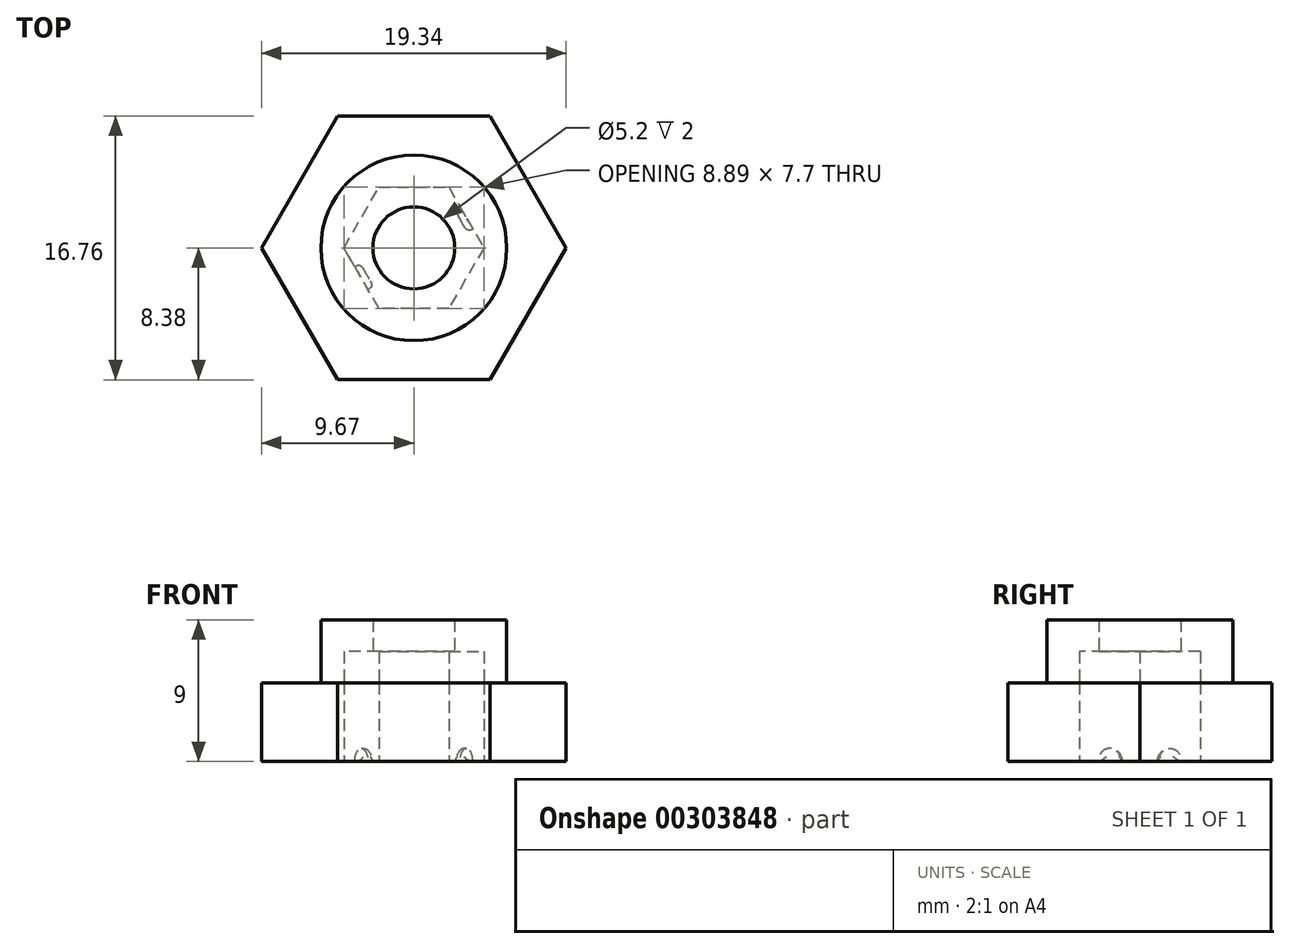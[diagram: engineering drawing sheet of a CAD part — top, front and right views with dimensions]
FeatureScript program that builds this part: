
annotation { "Feature Type Name" : "Feature", "Feature Type Description" : "" }
export const myFeature = defineFeature(function(context is Context, id is Id, definition is map)
    precondition{}
    {
        {
            var Q0;
            Q0=qCreatedBy(makeId("Top.planeOp"),FACE);
            var sketch = newSketch(context, id + "F0", { "sketchPlane" : qUnion([Q0])});
            skCircle(sketch, "E0.cCircle", {"center": v(0, 0) * mm, "radius": 8.38 * mm, "construction": true});
            skLineSegment(sketch, "E0.0", {"start": v(9.67, 0) * mm, "end": v(4.84, -8.38) * mm});
            skLineSegment(sketch, "E0.1", {"start": v(4.84, -8.38) * mm, "end": v(-4.84, -8.37) * mm});
            skLineSegment(sketch, "E0.2", {"start": v(-4.84, -8.38) * mm, "end": v(-9.67, 0) * mm});
            skLineSegment(sketch, "E0.3", {"start": v(-9.67, 0) * mm, "end": v(-4.84, 8.38) * mm});
            skLineSegment(sketch, "E0.4", {"start": v(-4.84, 8.37) * mm, "end": v(4.84, 8.37) * mm});
            skLineSegment(sketch, "E0.5", {"start": v(4.84, 8.38) * mm, "end": v(9.67, 0) * mm});
            skPoint(sketch, "E0.0.midPoint", {"position": v(7.25, -4.19) * mm});
            skCircle(sketch, "E1.cCircle", {"center": v(0, 0) * mm, "radius": 3.85 * mm, "construction": true});
            skLineSegment(sketch, "E1.0", {"start": v(4.45, 0) * mm, "end": v(2.22, -3.85) * mm});
            skLineSegment(sketch, "E1.1", {"start": v(2.22, -3.85) * mm, "end": v(-2.22, -3.85) * mm});
            skLineSegment(sketch, "E1.2", {"start": v(-2.22, -3.85) * mm, "end": v(-4.45, 0) * mm});
            skLineSegment(sketch, "E1.3", {"start": v(-4.45, 0) * mm, "end": v(-2.22, 3.85) * mm});
            skLineSegment(sketch, "E1.4", {"start": v(-2.22, 3.85) * mm, "end": v(2.22, 3.85) * mm});
            skLineSegment(sketch, "E1.5", {"start": v(2.22, 3.85) * mm, "end": v(4.45, 0) * mm});
            skPoint(sketch, "E1.0.midPoint", {"position": v(3.33, -1.93) * mm});
            skSolve(sketch);
        }
        {
            var Q0;
            Q0=makeQuery(id+"F0.imprint","IMPRINT",FACE,{"disambiguationData":[TD([[makeQuery(id+"F0.imprint","IMPRINT",EDGE,{"derivedFrom":sQuery(id+"F0.wireOp",EDGE,"E0.0")}),-1.0]])]});
            extrude(context, id + "F1", {"entities" : qUnion([Q0]), "depth" : 5 * mm});
        }
        {
            var Q0;
            Q0=makeQuery(id+"F1.opExtrude","CAP_FACE",FACE,{"disambiguationData":[OSD([sQuery(id+"F0.wireOp",EDGE,"E0.0"),sQuery(id+"F0.wireOp",EDGE,"E0.1"),sQuery(id+"F0.wireOp",EDGE,"E0.2"),sQuery(id+"F0.wireOp",EDGE,"E0.3"),sQuery(id+"F0.wireOp",EDGE,"E0.4"),sQuery(id+"F0.wireOp",EDGE,"E0.5"),sQuery(id+"F0.wireOp",EDGE,"E1.0"),sQuery(id+"F0.wireOp",EDGE,"E1.1"),sQuery(id+"F0.wireOp",EDGE,"E1.2"),sQuery(id+"F0.wireOp",EDGE,"E1.3"),sQuery(id+"F0.wireOp",EDGE,"E1.4"),sQuery(id+"F0.wireOp",EDGE,"E1.5")])],"isStart":false});
            var sketch = newSketch(context, id + "F2", { "sketchPlane" : qUnion([Q0])});
            skCircle(sketch, "E2", {"center": v(0, 0) * mm, "radius": 5.9 * mm});
            skSolve(sketch);
        }
        {
            var Q0;
            Q0=makeQuery(id+"F2.imprint","IMPRINT",FACE,{"disambiguationData":[TD([[makeQuery(id+"F2.imprint","IMPRINT",EDGE,{"derivedFrom":sQuery(id+"F2.wireOp",EDGE,"E2")}),1.0]])]});
            var Q1;
            Q1=sQuery(id+"F2.wireOp",EDGE,"E2");
            extrude(context, id + "F3", {"entities" : qUnion([Q0]), "surfaceEntities" : qUnion([Q1]), "depth" : 2 * mm});
        }
        {
            var Q0;
            Q0=makeQuery(id+"F3.opExtrude","CAP_FACE",FACE,{"disambiguationData":[OSD([sQuery(id+"F0.wireOp",EDGE,"E1.0"),sQuery(id+"F0.wireOp",EDGE,"E1.1"),sQuery(id+"F0.wireOp",EDGE,"E1.2"),sQuery(id+"F0.wireOp",EDGE,"E1.3"),sQuery(id+"F0.wireOp",EDGE,"E1.4"),sQuery(id+"F0.wireOp",EDGE,"E1.5"),sQuery(id+"F2.wireOp",EDGE,"E2")])],"isStart":false});
            var sketch = newSketch(context, id + "F4", { "sketchPlane" : qUnion([Q0])});
            skCircle(sketch, "E3", {"center": v(0, 0) * mm, "radius": 2.6 * mm});
            skSolve(sketch);
        }
        {
            var Q0;
            Q0=makeQuery(id+"F4.imprint","IMPRINT",FACE,{"disambiguationData":[TD([[makeQuery(id+"F4.imprint","IMPRINT",EDGE,{"derivedFrom":makeQuery(id+"F3.opExtrude","CAP_EDGE",EDGE,{"disambiguationData":[OSD([sQuery(id+"F2.wireOp",EDGE,"E2")])],"isStart":false})}),1.0]])]});
            var Q1;
            Q1=makeQuery(id+"F4.imprint","IMPRINT",FACE,{"disambiguationData":[TD([[makeQuery(id+"F4.imprint","IMPRINT",EDGE,{"derivedFrom":sQuery(id+"F4.wireOp",EDGE,"E3")}),-1.0]])]});
            extrude(context, id + "F5", {"entities" : qUnion([Q0, Q1]), "operationType" : NewBodyOperationType.ADD, "depth" : 2 * mm});
        }
        {
            var Q0;
            Q0=makeQuery(id+"F1.opExtrude","SWEPT_FACE",FACE,{"disambiguationData":[OSD([sQuery(id+"F0.wireOp",EDGE,"E1.2")])]});
            var sketch = newSketch(context, id + "F6", { "sketchPlane" : qUnion([Q0])});
            skCircle(sketch, "E4", {"center": v(0, 0) * mm, "radius": 0.84 * mm});
            skSolve(sketch);
        }
        {
            var Q0;
            {var subQ0=sQuery(id+"F6.wireOp",EDGE,"E4");var subQ1=makeQuery(id+"F1.opExtrude","CAP_EDGE",EDGE,{"disambiguationData":[OSD([sQuery(id+"F0.wireOp",EDGE,"E1.2")])],"isStart":true});var subQ2=makeQuery(id+"F6.imprint","INTERSECT",VERTEX,{"disambiguationData":[OD(0.0)],"derivedFrom":[subQ1,subQ0]});Q0=makeQuery(id+"F6.imprint","IMPRINT",FACE,{"disambiguationData":[TD([[makeQuery(id+"F6.imprint","IMPRINT",EDGE,{"disambiguationData":[TD([[subQ2,1.0]])],"derivedFrom":subQ0}),1.0]])]});}
            extrude(context, id + "F7", {"entities" : qUnion([Q0]), "operationType" : NewBodyOperationType.ADD, "depth" : 0.4 * mm});
        }
        {
            var Q0;
            Q0=makeQuery(id+"F7.opExtrude","CAP_FACE",FACE,{"disambiguationData":[OSD([sQuery(id+"F0.wireOp",EDGE,"E1.2"),sQuery(id+"F6.wireOp",EDGE,"E4")])],"isStart":false});
            fillet(context, id + "F8", {"entities" : qUnion([Q0]), "radius" : 0.3 * mm, "tangentPropagation" : true, "rho" : 0.5, "crossSection" : FilletCrossSection.CONIC, "allowEdgeOverflow" : false});
        }
        {
            var Q0;
            Q0=makeQuery(id+"F1.opExtrude","SWEPT_FACE",FACE,{"disambiguationData":[OSD([sQuery(id+"F0.wireOp",EDGE,"E1.5")])]});
            var sketch = newSketch(context, id + "F9", { "sketchPlane" : qUnion([Q0])});
            skCircle(sketch, "E5", {"center": v(0, 0) * mm, "radius": 0.84 * mm});
            skSolve(sketch);
        }
        {
            var Q0;
            {var subQ0=sQuery(id+"F9.wireOp",EDGE,"E5");var subQ1=makeQuery(id+"F1.opExtrude","CAP_EDGE",EDGE,{"disambiguationData":[OSD([sQuery(id+"F0.wireOp",EDGE,"E1.5")])],"isStart":true});var subQ2=makeQuery(id+"F9.imprint","INTERSECT",VERTEX,{"disambiguationData":[OD(0.0)],"derivedFrom":[subQ1,subQ0]});Q0=makeQuery(id+"F9.imprint","IMPRINT",FACE,{"disambiguationData":[TD([[makeQuery(id+"F9.imprint","IMPRINT",EDGE,{"disambiguationData":[TD([[subQ2,-1.0]])],"derivedFrom":subQ0}),1.0]])]});}
            extrude(context, id + "F10", {"entities" : qUnion([Q0]), "depth" : 0.4 * mm});
        }
        {
            var Q0;
            Q0=makeQuery(id+"F10.opExtrude","CAP_FACE",FACE,{"disambiguationData":[OSD([sQuery(id+"F0.wireOp",EDGE,"E1.5"),sQuery(id+"F9.wireOp",EDGE,"E5")])],"isStart":false});
            fillet(context, id + "F11", {"entities" : qUnion([Q0]), "radius" : 0.3 * mm, "tangentPropagation" : true, "allowEdgeOverflow" : false});
        }
    });
